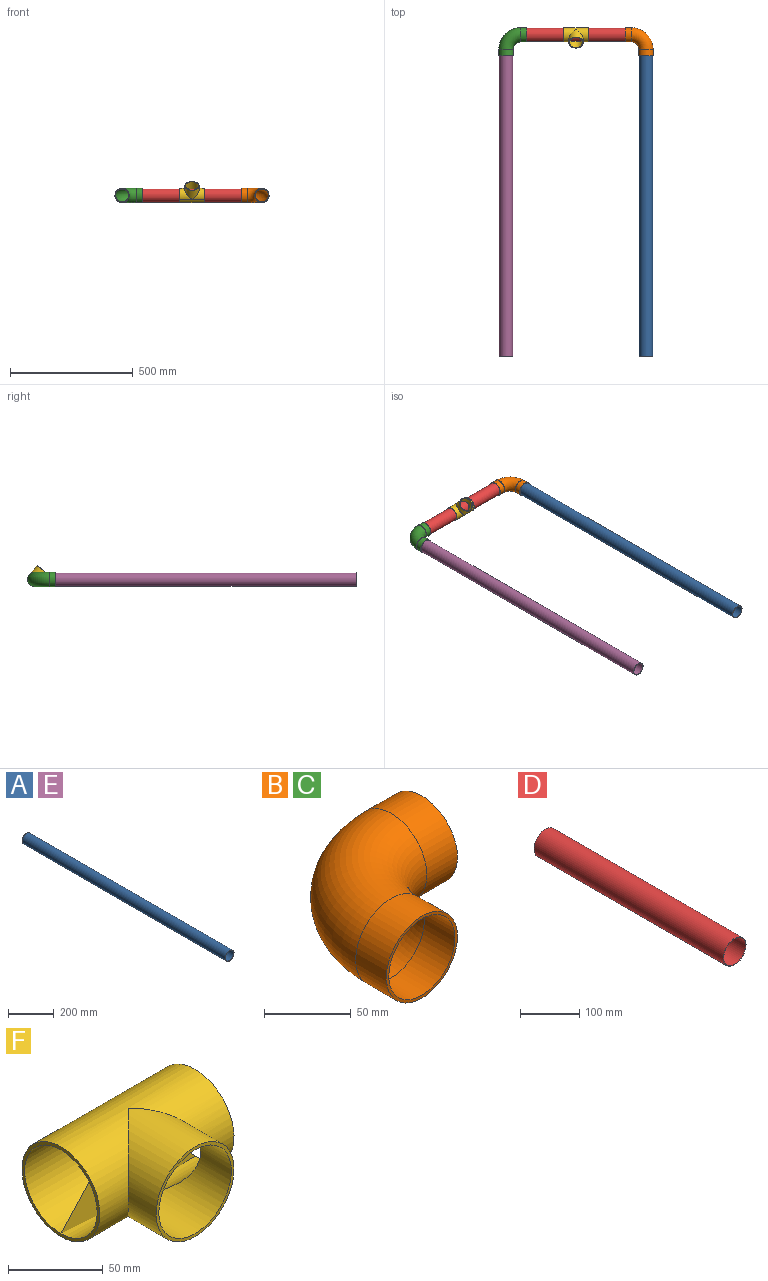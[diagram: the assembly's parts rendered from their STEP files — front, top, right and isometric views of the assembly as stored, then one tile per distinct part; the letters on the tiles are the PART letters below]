
ASSEMBLY  parts=6 mates=5
PART A: 4 faces, bbox 54x1250x54 mm
  f0: cylinder r=26mm len=1250mm, axis (0,1,0), area 204203.5mm2, adj f2,f3
  f1: cylinder r=27mm len=1250mm, axis (0,1,0), area 212057.5mm2, adj f2,f3
  f2: plane 54x54mm, normal (0,-1,0), area 166.5mm2, adj f0,f1
  f3: plane 54x54mm, normal (0,1,0), area 166.5mm2, adj f0,f1
PART B: 8 faces, bbox 121.3x121.3x58 mm
  f0: torus R=60mm, axis (0,0,1), area 15988.8mm2, adj f2,f5
  f1: torus R=60mm, axis (0,0,1), area 17173.1mm2, adj f3,f6
  f2: cylinder r=27mm len=54mm, axis (0,1,0), area 4241.2mm2, adj f0,f4
  f3: cylinder r=29mm len=58mm, axis (0,1,0), area 4555.3mm2, adj f1,f4
  f4: plane 58x58mm, normal (0,-1,0), area 351.9mm2, adj f2,f3
  f5: cylinder r=27mm len=54mm, axis (-1,0,0), area 4241.2mm2, adj f0,f7
  f6: cylinder r=29mm len=58mm, axis (-1,0,0), area 4555.3mm2, adj f1,f7
  f7: plane 58x58mm, normal (1,0,0), area 351.9mm2, adj f5,f6
PART C: same geometry as B
PART D: 4 faces, bbox 54x450x54 mm
  f0: cylinder r=26mm len=450mm, axis (0,1,0), area 73513.3mm2, adj f2,f3
  f1: cylinder r=27mm len=450mm, axis (0,1,0), area 76340.7mm2, adj f2,f3
  f2: plane 54x54mm, normal (0,-1,0), area 166.5mm2, adj f0,f1
  f3: plane 54x54mm, normal (0,1,0), area 166.5mm2, adj f0,f1
PART E: same geometry as A
PART F: 7 faces, bbox 100x79x58 mm
  f0: cylinder r=29mm len=100mm, axis (-1,0,0), area 14857.2mm2, adj f1,f2,f4
  f1: plane 58x58mm, normal (1,0,0), area 351.9mm2, adj f0,f6
  f2: plane 58x58mm, normal (-1,0,0), area 351.9mm2, adj f0,f6
  f3: plane 58x58mm, normal (0,-1,0), area 351.9mm2, adj f4,f5
  f4: cylinder r=29mm len=58mm, axis (0,1,0), area 5746.6mm2, adj f0,f3
  f5: cylinder r=27mm len=54mm, axis (0,1,0), area 5566.3mm2, adj f3,f6
  f6: cylinder r=27mm len=100mm, axis (-1,0,0), area 14048.6mm2, adj f1,f2,f5
PLACE A t=(278.7,316.58,-210.36)mm
PLACE B rot(axis=(0,0,-1),90deg) t=(218.7,376.58,-210.36)mm
PLACE C t=(-291.3,316.58,-210.36)mm
PLACE D rot(axis=(0,0,-1),90deg) t=(218.7,376.58,-210.36)mm
PLACE E t=(-291.3,316.58,-210.36)mm fixed
PLACE F rot(axis=(-1,0,0),50.4deg) t=(-6.3,376.58,-210.36)mm
MATE fastened C.f3 <-> E.f0  axis (0,1,0) through (-291.3,316.58,-210.36)mm
MATE fastened D.f0 <-> C.f5  axis (1,0,0) through (-231.3,376.58,-210.36)mm
MATE fastened B.f3 <-> D.f0  axis (1,0,0) through (218.7,376.58,-210.36)mm
MATE revolute F.f0 <-> D.f1  axis (-1,0,0) through (-6.3,376.58,-210.36)mm
MATE fastened A.f0 <-> B.f5  axis (0,1,0) through (278.7,316.58,-210.36)mm
